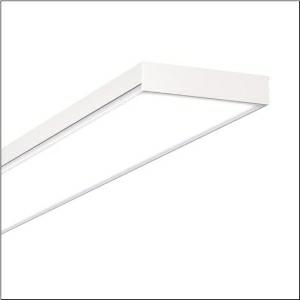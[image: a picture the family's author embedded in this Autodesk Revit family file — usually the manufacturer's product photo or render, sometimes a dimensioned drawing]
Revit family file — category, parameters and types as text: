
# Revit family: apollon_r__31_51mp25wd2341w_0334
name_source: partatom
category: Lighting Fixtures
units: mm (PartAtom-declared; Revit-internal decimal feet)

## family parameters
Cut with Voids When Loaded = No
Host = Face
Light Source = No
Part Type = Normal
Room Calculation Point = No
Round Connector Dimension = Use Diameter
Shared = No

## types (1)
- Apollon® 31 (1 x LED, 3600 lm, 28 W, 3000K)
    Apparent Load = 28 VA
    CIE Flux Codes = 61 87 97 97 100
    Color Rendering = 80
    Color Temperature = 3000K
    Default Elevation = 1800 mm
    Description = Apollon® 31, office luminaire, primary optical cover: micro prismatic cover, of PMMA, light emission: direct distribution, primary light characteristic: symmetric, installation type: surface-mounted, LED, rated luminous flux: 3.600lm, luminous efficacy: 128lm/W, light colour: 830, colour temperature: 3000K, control gear: ECG DALI, with terminal, 5-pole, mains connection: 220..240V, AC, 50/60Hz, rated input power: 28W, housing, of sheet steel, coil coated, traffic white (RAL 9016), length: 1.245mm, width: 200mm, height: 44mm, protection rating (complete): IP20, insulation class (complete): insulation class II (safety insulation), certification: CE, impact resistance: IK02, permissible operating ambient temperature: -20..+40°C, standard: EN 60598-2-22, packaging unit: 1 piece
    Height = 44 mm
    Lamp = 1 x LED
    Lamp Light Flux = 3600 lm
    Lamp Power = 28 W
    Lamp count = 1
    Length = 1245 mm
    Luminous efficacy = 129 lm/W
    Manufacturer = Siteco
    ModVariant = No
    Model = 51MP25WD2341W
    Mounting Place = Ceiling
    Mounting Type = Surface mounted
    Number of Poles = 1
    OnlyDefault = Yes
    Power Factor = 1
    Product Name = Apollon® 31
    Product group = office luminaire | ceiling mounted
    ProductGroupID = 302
    Protection Class = Protection class II
    Protection Degree = IP 20
    RLX_Detail_Level = 1
    RlxData = <blob elided: 20729 chars, md5=51f22646>
    Socket = socket
    Standby Power = 0 W
    System Light Flux = 3600 lm
    System Power = 28 W
    Type Comments = Product without accessories
    Type Image = l_1007095.jpg
    URL = http://relux.com
    VarID = ---
    Voltage = 0 V
    Weight = 0.00 kg
    Width = 200 mm  [stored 0.656168 ft]

note: [stored X ft] marks values corroborated as IEEE doubles in the binary element streams (Revit-internal decimal feet)

## geometry (parser evidence)
native form markers: Blend x4, Sweep x9
no freeform markers — native parametric forms only
